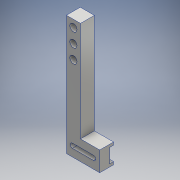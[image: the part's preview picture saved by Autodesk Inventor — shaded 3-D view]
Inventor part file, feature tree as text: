
AUTODESK INVENTOR PART (.ipt)
format: ipt  version: 2016 (Build 200138000, 138)  size: 150,528 bytes
history: native  units: mm
features: extrude x5, sketch x4
ambient origin geometry x8: Origin, YZ Plane, XZ Plane, XY Plane, X Axis, Y Axis, Z Axis, Center Point
bodies: Solid1 (feature_tree)
feature tree (9):
  extrude  "Extrusion1"  Depth=108.0mm
  extrude  "Extrusion2"  Depth=90.2mm
  extrude  "Extrusion3"  Depth=12.8mm
  sketch  "Sketch4"  dims[d7=3.5mm d8=0.0mm d9=4.0mm d10=4.0mm d11=3.5mm d12=0.0mm d13=11.0mm d14=11.0mm d15=11.0mm d16=12.5mm d17=12.5mm d18=6.5mm d19=6.5mm d20=6.5mm d21=3.5mm d22=0.0mm d23=6.0mm d24=0.0mm d25=6.5mm]
  extrude  "Extrusion4"  Depth=4.0mm
  extrude  "Extrusion5"  Depth=4.0mm
  sketch  "Sketch1"  dims[d0=30.0mm d1=108.0mm]
  sketch  "Sketch2"  dims[d2=12.7mm d3=90.2mm]
  sketch  "Sketch3"  dims[d4=12.5mm d5=0.0mm d6=12.8mm]
